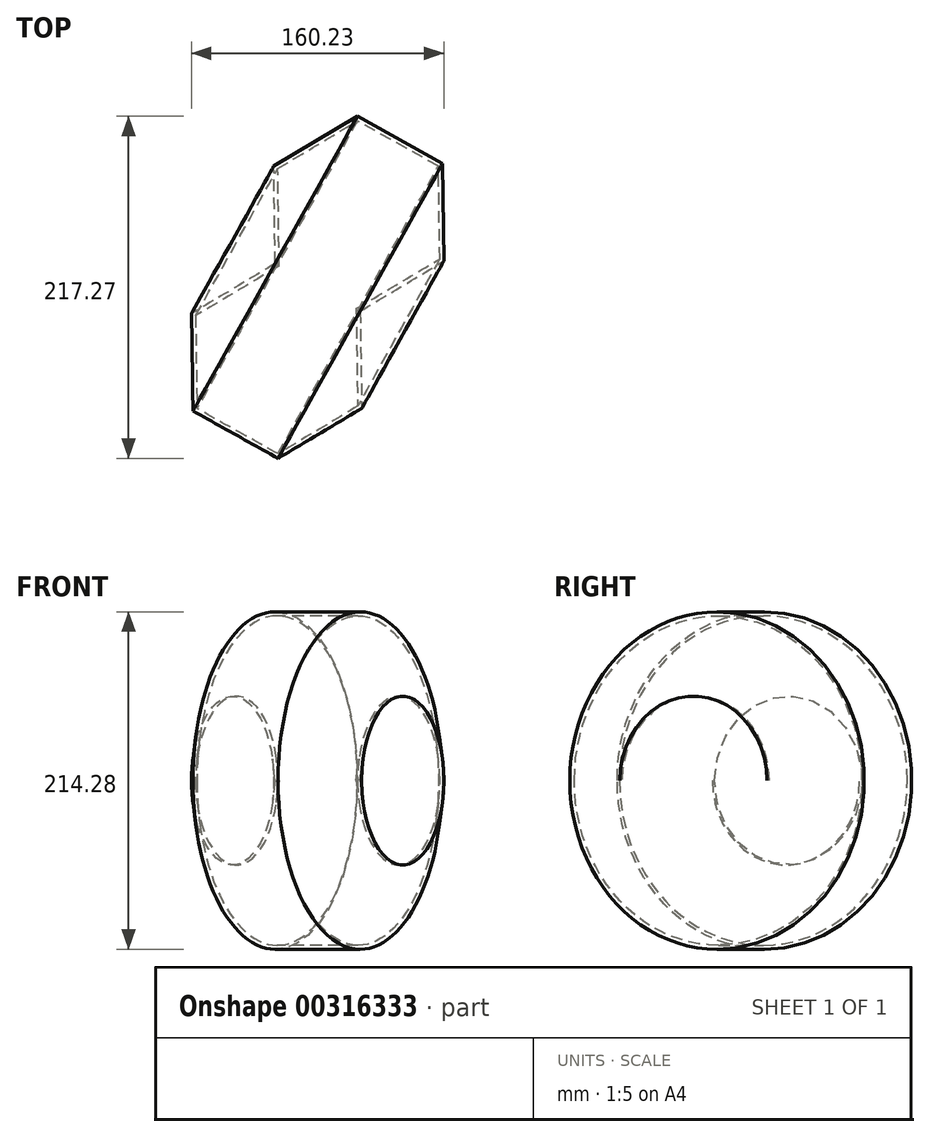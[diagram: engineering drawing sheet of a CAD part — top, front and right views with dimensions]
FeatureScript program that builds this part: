
annotation { "Feature Type Name" : "Feature", "Feature Type Description" : "" }
export const myFeature = defineFeature(function(context is Context, id is Id, definition is map)
    precondition{}
    {
        {
            var Q0;
            Q0=qCreatedBy(makeId("Top.planeOp"),FACE);
            var sketch = newSketch(context, id + "F0", { "sketchPlane" : qUnion([Q0])});
            skCircle(sketch, "E0.cCircle", {"center": v(0, 0) * mm, "radius": 53.57 * mm, "construction": true});
            skLineSegment(sketch, "E0.0", {"start": v(-54.02, 30.13) * mm, "end": v(-0.92, 61.85) * mm});
            skLineSegment(sketch, "E0.1", {"start": v(-0.92, 61.85) * mm, "end": v(53.1, 31.72) * mm});
            skLineSegment(sketch, "E0.2", {"start": v(53.1, 31.72) * mm, "end": v(54.02, -30.13) * mm});
            skLineSegment(sketch, "E0.3", {"start": v(54.02, -30.13) * mm, "end": v(0.92, -61.85) * mm});
            skLineSegment(sketch, "E0.4", {"start": v(0.92, -61.85) * mm, "end": v(-53.1, -31.72) * mm});
            skLineSegment(sketch, "E0.5", {"start": v(-53.1, -31.72) * mm, "end": v(-54.02, 30.13) * mm});
            skPoint(sketch, "E0.0.midPoint", {"position": v(-27.47, 46) * mm});
            skSolve(sketch);
        }
        {
            var Q0;
            Q0=makeQuery(id+"F0.imprint","IMPRINT",FACE,{"disambiguationData":[TD([[makeQuery(id+"F0.imprint","IMPRINT",EDGE,{"derivedFrom":sQuery(id+"F0.wireOp",EDGE,"E0.0")}),-1.0]])]});
            var Q1;
            Q1=sQuery(id+"F0.wireOp",EDGE,"E0.1");
            revolve(context, id + "F1", {"entities" : qUnion([Q0]), "axis" : qUnion([Q1]), "revolveType" : RevolveType.FULL});
        }
        {
            var Q0;
            Q0=makeQuery(id+"F1.opRevolve","SWEPT_FACE",FACE,{"disambiguationData":[OSD([sQuery(id+"F0.wireOp",EDGE,"E0.2")])]});
            var Q1;
            Q1=makeQuery(id+"F1.opRevolve","SWEPT_BODY",BODY,{"disambiguationData":[OSD([sQuery(id+"F0.wireOp",EDGE,"E0.0"),sQuery(id+"F0.wireOp",EDGE,"E0.1"),sQuery(id+"F0.wireOp",EDGE,"E0.2"),sQuery(id+"F0.wireOp",EDGE,"E0.3"),sQuery(id+"F0.wireOp",EDGE,"E0.4"),sQuery(id+"F0.wireOp",EDGE,"E0.5")])]});
            shell(context, id + "F2", {"isHollow" : true, "entities" : qUnion([Q0]), "parts" : qUnion([Q1]), "thickness" : 2.54 * mm});
        }
    });
